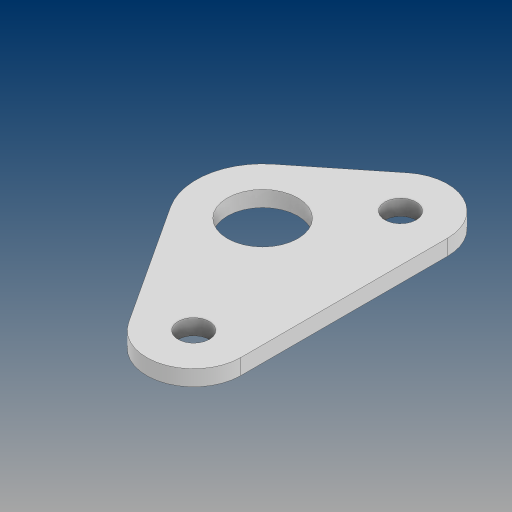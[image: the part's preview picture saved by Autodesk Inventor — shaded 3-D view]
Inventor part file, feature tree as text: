
AUTODESK INVENTOR PART (.ipt)
format: ipt  version: 2024.3 (Build 283343000, 343)  size: 113,152 bytes
history: native  units: in
note: dims shown in document units (in); Inventor stores cm internally (conversion verified against a paired STEP export)
features: extrude x1, sketch x1
ambient origin geometry x8: Origin, YZ Plane, XZ Plane, XY Plane, X Axis, Y Axis, Z Axis, Center Point
bodies: Solid1 (feature_tree)
feature tree (2):
  extrude  "Extrusion1"  Depth=0.25in
  sketch  "Sketch1"  dims[d0=3.3in d1=0.5in d2=0.5in d4=1.125in d5=1.2in d6=0.5in d7=1.0in d8=0.5in d9=0.5in d10=0.25in d11=0.0in]
